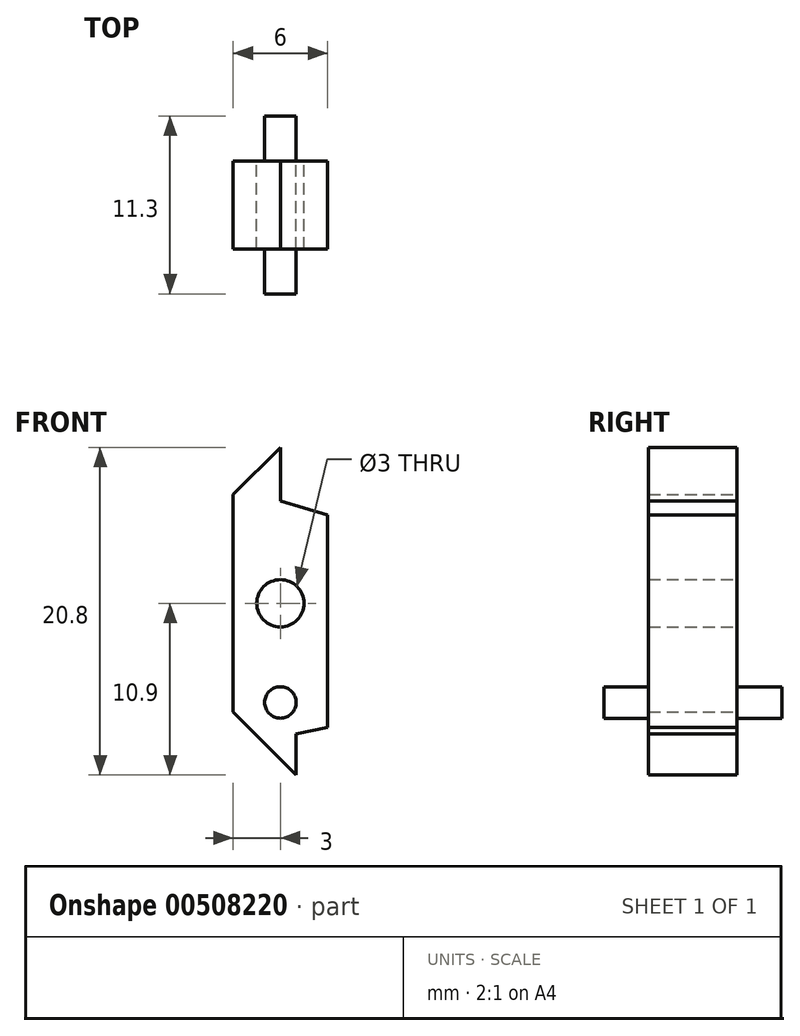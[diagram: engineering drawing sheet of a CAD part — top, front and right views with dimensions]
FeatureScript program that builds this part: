
annotation { "Feature Type Name" : "Feature", "Feature Type Description" : "" }
export const myFeature = defineFeature(function(context is Context, id is Id, definition is map)
    precondition{}
    {
        {
            var Q0;
            Q0=qCreatedBy(makeId("Front.planeOp"),FACE);
            var sketch = newSketch(context, id + "F0", { "sketchPlane" : qUnion([Q0])});
            skLineSegment(sketch, "E0", {"start": v(-3, 6.9) * mm, "end": v(-3, -6.9) * mm});
            skLineSegment(sketch, "E1", {"start": v(-3, -6.9) * mm, "end": v(1, -10.9) * mm});
            skLineSegment(sketch, "E2", {"start": v(1, -10.9) * mm, "end": v(1, -8.3) * mm});
            skLineSegment(sketch, "E3", {"start": v(1, -8.3) * mm, "end": v(3, -7.9) * mm});
            skLineSegment(sketch, "E4", {"start": v(3, -7.9) * mm, "end": v(3, 5.6) * mm});
            skLineSegment(sketch, "E5", {"start": v(3, 5.6) * mm, "end": v(0, 6.5) * mm});
            skLineSegment(sketch, "E6", {"start": v(0, 6.5) * mm, "end": v(0, 9.9) * mm});
            skLineSegment(sketch, "E7", {"start": v(0, 9.9) * mm, "end": v(-3, 6.9) * mm});
            skCircle(sketch, "E8", {"center": v(0, 0) * mm, "radius": 1.5 * mm});
            skLineSegment(sketch, "E9", {"start": v(0, 0) * mm, "end": v(-3, 0) * mm, "construction": true});
            skCircle(sketch, "E10", {"center": v(0, -6.3) * mm, "radius": 1 * mm});
            skSolve(sketch);
        }
        {
            var Q0;
            Q0=makeQuery(id+"F0.imprint","IMPRINT",FACE,{"disambiguationData":[TD([[makeQuery(id+"F0.imprint","IMPRINT",EDGE,{"derivedFrom":sQuery(id+"F0.wireOp",EDGE,"E0")}),1.0]])]});
            extrude(context, id + "F1", {"entities" : qUnion([Q0]), "depth" : 5.6 * mm, "offsetDistance" : 25 * mm, "symmetric" : true});
        }
        {
            var Q0;
            Q0=makeQuery(id+"F0.imprint","IMPRINT",FACE,{"disambiguationData":[TD([[makeQuery(id+"F0.imprint","IMPRINT",EDGE,{"derivedFrom":sQuery(id+"F0.wireOp",EDGE,"E10")}),1.0]])]});
            extrude(context, id + "F2", {"entities" : qUnion([Q0]), "operationType" : NewBodyOperationType.ADD, "depth" : 11.3 * mm, "offsetDistance" : 25 * mm, "symmetric" : true});
        }
    });
